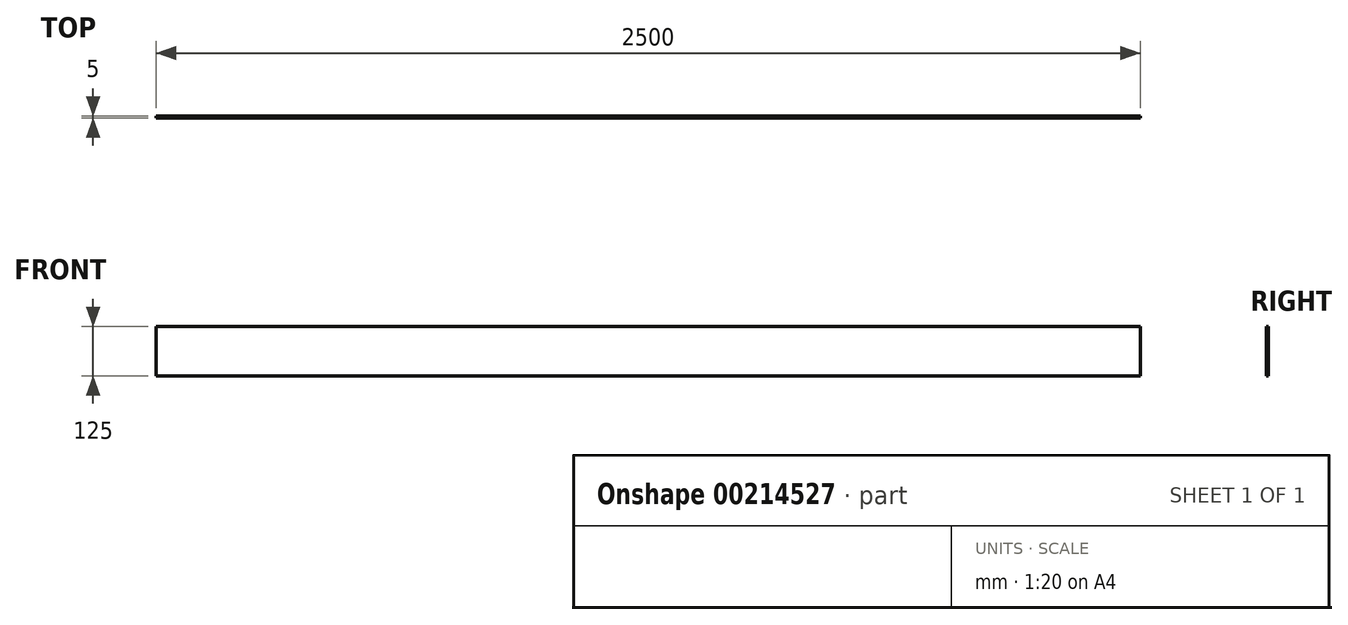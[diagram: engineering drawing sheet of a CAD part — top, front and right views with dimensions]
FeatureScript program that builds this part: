
annotation { "Feature Type Name" : "Feature", "Feature Type Description" : "" }
export const myFeature = defineFeature(function(context is Context, id is Id, definition is map)
    precondition{}
    {
        {
            var Q0;
            Q0=qCreatedBy(makeId("Front.planeOp"),FACE);
            var sketch = newSketch(context, id + "F0", { "sketchPlane" : qUnion([Q0])});
            skLineSegment(sketch, "E0.bottom", {"start": v(-1250, 62.5) * mm, "end": v(1250, 62.5) * mm});
            skLineSegment(sketch, "E0.top", {"start": v(-1250, -62.5) * mm, "end": v(1250, -62.5) * mm});
            skLineSegment(sketch, "E0.left", {"start": v(-1250, 62.5) * mm, "end": v(-1250, -62.5) * mm});
            skLineSegment(sketch, "E0.right", {"start": v(1250, 62.5) * mm, "end": v(1250, -62.5) * mm});
            skSolve(sketch);
        }
        {
            var Q0;
            Q0 = qSketchRegion(id + "F0", true);
            extrude(context, id + "F1", {"entities" : qUnion([Q0]), "depth" : 5 * mm});
        }
    });
